# Revit family: Sanitary_Accessories_Svedholm_Slits-toilet-brush
name_source: partatom
category: Furniture
revit_build: Autodesk Revit 2018 (Build: 20170223_1515(x64)
units: mm (PartAtom-declared; Revit-internal decimal feet)

## family parameters
Cut with Voids When Loaded = No
Host = Face
OmniClass Number = 23.21.11.00
OmniClass Title = Commercial Furniture
Room Calculation Point = No
Shared = No

## types (1)
- ART - (410.600.030)
    BIMobject category = Accessories
    Default Elevation = 1219 mm
    Description = A toilet brush made of powder coated steel.
    Detail matrial = Svedholm - Plastic - Black
    Edition number = 1
    IFC Classification = Object
    Manufacturer = Svedholm
    Manufacturer name = Svedholm
    Model = Slits toilet brush
    OmniClass Code = 23-21 11 00
    OmniClass Description = Commercial Furniture
    Product Guid = e3f14ec5-f0ce-444d-b658-12bcccf98d00
    Product SKU = Slits-toilet-brush
    Product data url = https://bimobject.com
    Product family = Slits
    Product group = Accessories
    Product name = Slits toilet brush
    Product url = https://www.svedholm.se
    QR code = https://bimobject.com
    Secondary material = Svedholm - Metal - Stainless Steel
    URL = https://www.svedholm.se
    Uniclass 2015 Code = Zz_30_60
    Uniclass 2015 Name = Objects

## geometry (parser evidence)
native form markers: Sweep x3
no freeform markers — native parametric forms only
